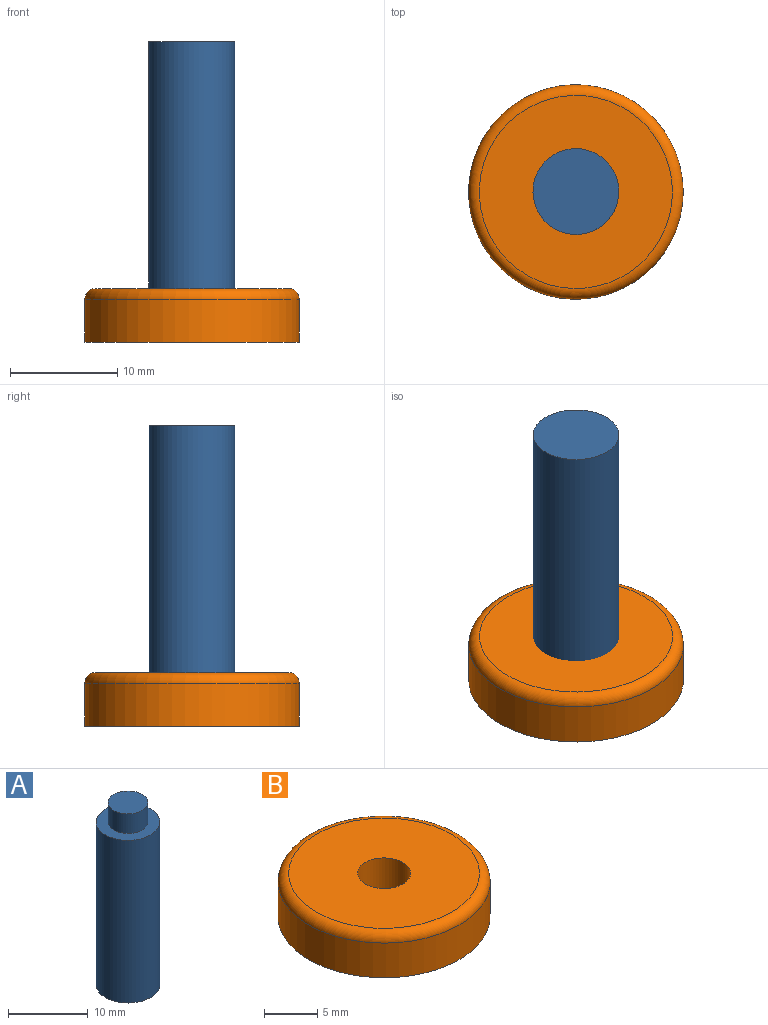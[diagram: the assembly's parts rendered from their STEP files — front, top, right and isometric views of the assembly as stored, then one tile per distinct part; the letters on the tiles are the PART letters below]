
ASSEMBLY  parts=2 mates=1
PART A: 5 faces, bbox 8x8x28 mm
  f0: cylinder r=4mm len=25mm, axis (0,0,-1), area 628.3mm2, adj f1,f2
  f1: plane 8x8mm, normal (0,0,1), area 30.6mm2, adj f0,f3
  f2: plane 8x8mm, normal (0,0,-1), area 50.3mm2, adj f0
  f3: cylinder r=2.5mm len=5mm, axis (0,0,-1), area 47.1mm2, adj f1,f4
  f4: plane 5x5mm, normal (0,0,1), area 19.6mm2, adj f3
PART B: 5 faces, bbox 21.6x21.6x5 mm
  f0: cylinder r=2.5mm len=5mm, axis (0,0,-1), area 78.5mm2, adj f2,f3
  f1: cylinder r=10mm len=20mm, axis (0,0,-1), area 251.3mm2, adj f3,f4
  f2: plane 18x18mm, normal (0,0,1), area 234.8mm2, adj f0,f4
  f3: plane 20x20mm, normal (0,0,-1), area 294.5mm2, adj f0,f1
  f4: torus R=9mm, axis (0,0,1), area 95.1mm2, adj f1,f2
PLACE A rot(axis=(0.77,-0.64,0),180deg) t=(-10.28,0.65,23.88)mm
PLACE B t=(-10.28,0.65,-4.12)mm fixed
MATE revolute B.f0 <-> A.f3  axis (0,0,-1) through (-10.28,0.65,-4.12)mm
